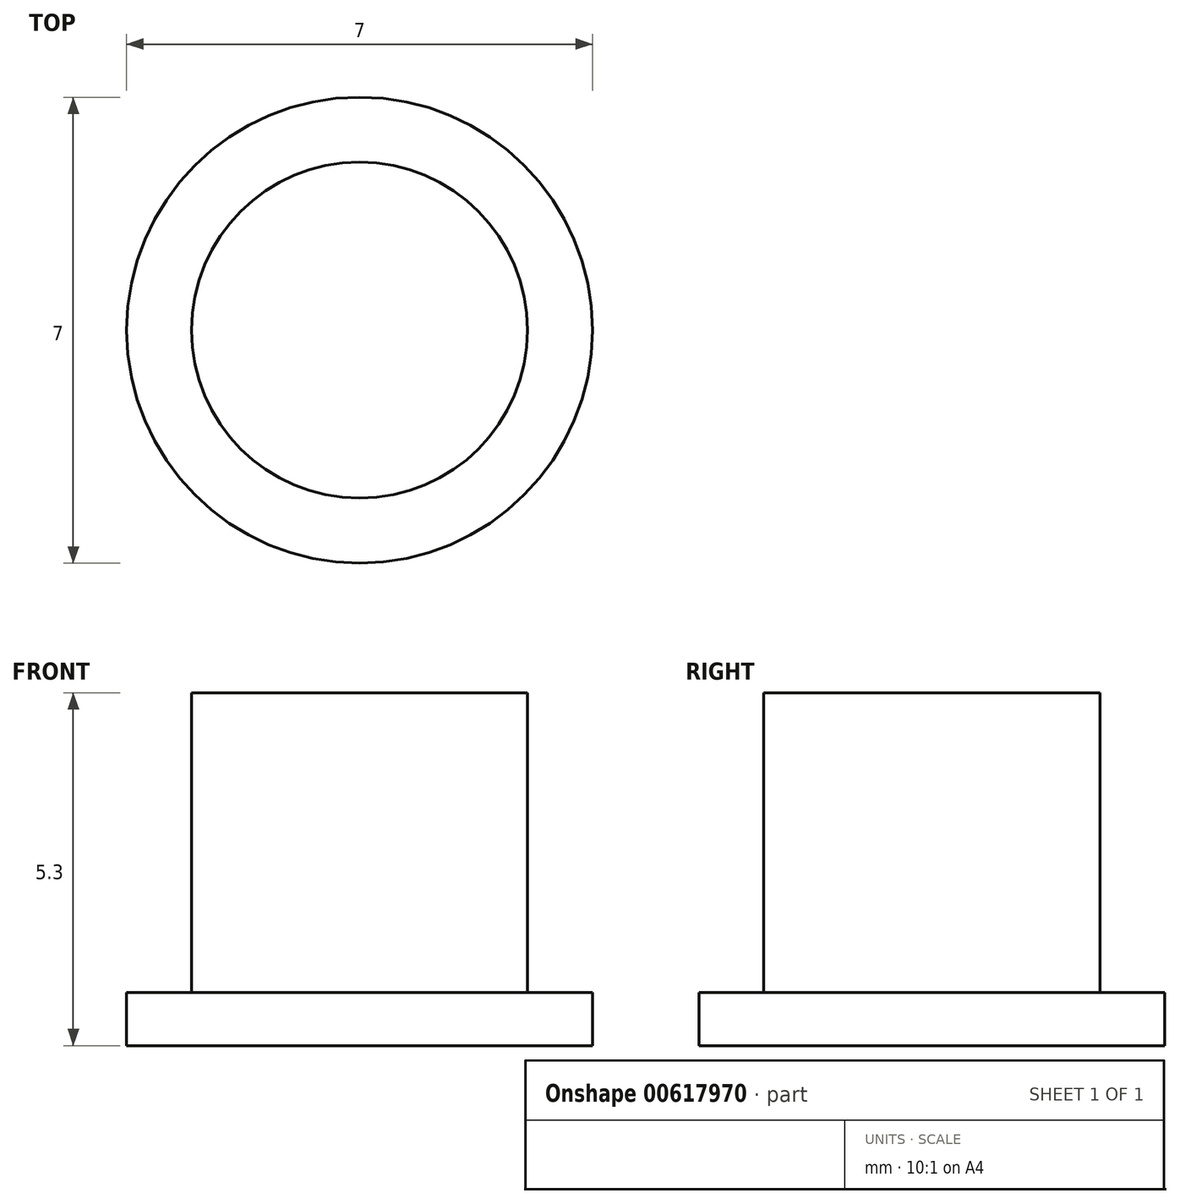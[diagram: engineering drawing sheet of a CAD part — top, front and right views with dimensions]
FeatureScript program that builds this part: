
annotation { "Feature Type Name" : "Feature", "Feature Type Description" : "" }
export const myFeature = defineFeature(function(context is Context, id is Id, definition is map)
    precondition{}
    {
        {
            var Q0;
            Q0=qCreatedBy(makeId("Top.planeOp"),FACE);
            var sketch = newSketch(context, id + "F0", { "sketchPlane" : qUnion([Q0])});
            skCircle(sketch, "E0", {"center": v(0, 0) * mm, "radius": 2.52 * mm});
            skCircle(sketch, "E1", {"center": v(0, 0) * mm, "radius": 3.5 * mm});
            skSolve(sketch);
        }
        {
            var Q0;
            Q0=makeQuery(id+"F0.imprint","IMPRINT",FACE,{"disambiguationData":[TD([[makeQuery(id+"F0.imprint","IMPRINT",EDGE,{"derivedFrom":sQuery(id+"F0.wireOp",EDGE,"E0")}),-1.0]])]});
            extrude(context, id + "F1", {"entities" : qUnion([Q0]), "depth" : .8 * mm, "offsetDistance" : 25 * mm});
        }
        {
            var Q0;
            Q0=makeQuery(id+"F0.imprint","IMPRINT",FACE,{"disambiguationData":[TD([[makeQuery(id+"F0.imprint","IMPRINT",EDGE,{"derivedFrom":sQuery(id+"F0.wireOp",EDGE,"E0")}),1.0]])]});
            extrude(context, id + "F2", {"entities" : qUnion([Q0]), "operationType" : NewBodyOperationType.ADD, "depth" : 5.3 * mm, "offsetDistance" : 25 * mm});
        }
        {
            var Q0;
            Q0=qCreatedBy(makeId("Front.planeOp"),FACE);
            var sketch = newSketch(context, id + "F3", { "sketchPlane" : qUnion([Q0])});
            skLineSegment(sketch, "E2", {"start": v(0, 0) * mm, "end": v(0, -0.8) * mm});
            skLineSegment(sketch, "E3", {"start": v(0, -0.8) * mm, "end": v(-1.25, 0) * mm});
            skLineSegment(sketch, "E4", {"start": v(-1.25, 0) * mm, "end": v(0, 0) * mm});
            skSolve(sketch);
        }
        {
            var Q0;
            Q0=sQuery(id+"F3.wireOp",EDGE,"E3");
            var Q1;
            Q1=sQuery(id+"F3.wireOp",EDGE,"E4");
            var Q2;
            Q2=sQuery(id+"F3.wireOp",EDGE,"E2");
            revolve(context, id + "F4", {"bodyType" : ToolBodyType.SURFACE, "surfaceEntities" : qUnion([Q0, Q1]), "axis" : qUnion([Q2]), "revolveType" : RevolveType.FULL});
        }
    });
